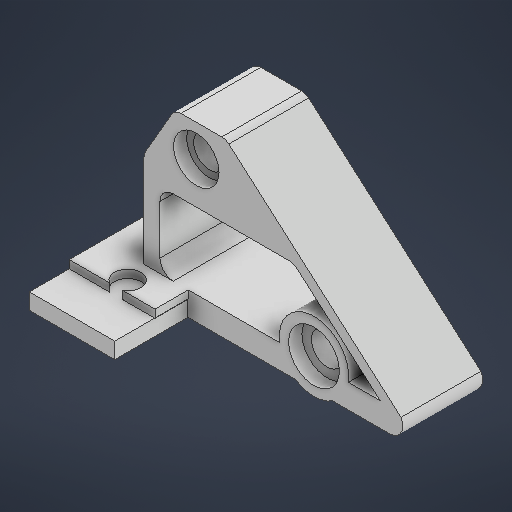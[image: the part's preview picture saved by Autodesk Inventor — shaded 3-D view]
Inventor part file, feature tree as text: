
AUTODESK INVENTOR PART (.ipt)
format: ipt  version: 2025.3 (Build 293356000, 356)  size: 519,168 bytes
history: native  units: in
note: dims shown in document units (in); Inventor stores cm internally (conversion verified against a paired STEP export)
features: extrude x15, fillet x8, sketch x7, projected_geometry x5, other x3
ambient origin geometry x8: Origin, YZ Plane, XZ Plane, XY Plane, X Axis, Y Axis, Z Axis, Center Point
bodies: Solid1 (feature_tree)
feature tree (38):
  other  "EngineMount - Big hole.ipt"
  sketch  "Sketch1"  dims[d0=0.3937in d2=0.2362in]
  extrude  "Extrusion1"  Depth=0.2362in
  extrude  "Extrusion2"  Depth=0.2362in TaperAngle=0.0deg
  fillet  "Fillet2"  Radius=0.3937in
  fillet  "Fillet3"  Radius=0.1969in
  sketch  "Sketch2"  dims[d3=0.2362in d4=0.2362in d5=0.0in d6=0.3937in d7=0.0in d9=0.1969in]
  extrude  "Extrusion3"  Depth=0.1969in
  extrude  "Extrusion4"  Depth=0.3937in TaperAngle=0.0deg
  sketch  "Sketch4"  dims[d10=0.1969in d11=0.5512in]
  extrude  "Extrusion10"  Depth=1.1811in
  extrude  "Extrusion11"  Depth=0.1969in TaperAngle=0.0deg
  extrude  "Extrusion12"  Depth=0.2362in
  extrude  "Extrusion13"  Depth=0.2362in
  extrude  "Extrusion14"  Depth=0.3937in TaperAngle=0.0deg
  extrude  "Extrusion15"  Depth=0.2362in
  sketch  "Sketch8"  dims[d41=0.1969in d42=1.9685in d43=0.0in]
  extrude  "Extrusion16"  Depth=0.3937in TaperAngle=0.0deg
  extrude  "Extrusion17"  Depth=0.1181in
  fillet  "Fillet5"  Radius=1.1811in
  fillet  "Fillet6"  Radius=1.0827in
  fillet  "Fillet7"  Radius=1.1811in
  fillet  "Fillet8"  Radius=0.2362in
  sketch  "Sketch9"  dims[d44=0.1969in d45=0.2362in d46=0.2362in d47=0.3937in d48=0.0in d49=0.2362in d50=0.3937in d51=0.0in d52=0.1181in d53=1.1811in d54=0.0in d56=1.0827in d57=0.0in d58=1.1811in d59=0.0in d60=0.2362in d61=1.7717in d62=1.1811in d63=0.0in d64=0.1969in d65=0.1969in d66=0.1969in d67=0.1969in d68=0.1575in d69=0.3937in d70=0.0in d71=1.1811in d72=0.0in d73=1.1811in d74=0.0in d75=0.1575in d76=0.1575in]
  extrude  "Extrusion18"  Depth=0.1575in
  extrude  "Extrusion19"  Depth=1.1811in TaperAngle=0.0deg
  extrude  "Extrusion20"  Depth=0.1969in
  fillet  "Fillet9"  Radius=0.1969in
  fillet  "Fillet10"  Radius=0.1969in
  other  "Solid1::EngineMount - Big hole.ipt"
  other  "TaggingFeature1"
  projected_geometry  "Projected Loop1"
  projected_geometry  "Projected Loop2"
  projected_geometry  "Projected Loop4"
  sketch  "Sketch6"  dims[d12=0.3937in d13=0.0in d14=0.3937in d15=0.0in]
  sketch  "Sketch7"  dims[d38=1.9685in d39=0.0in d40=1.1811in]
  projected_geometry  "Projected Loop6"
  projected_geometry  "Projected Loop7"
